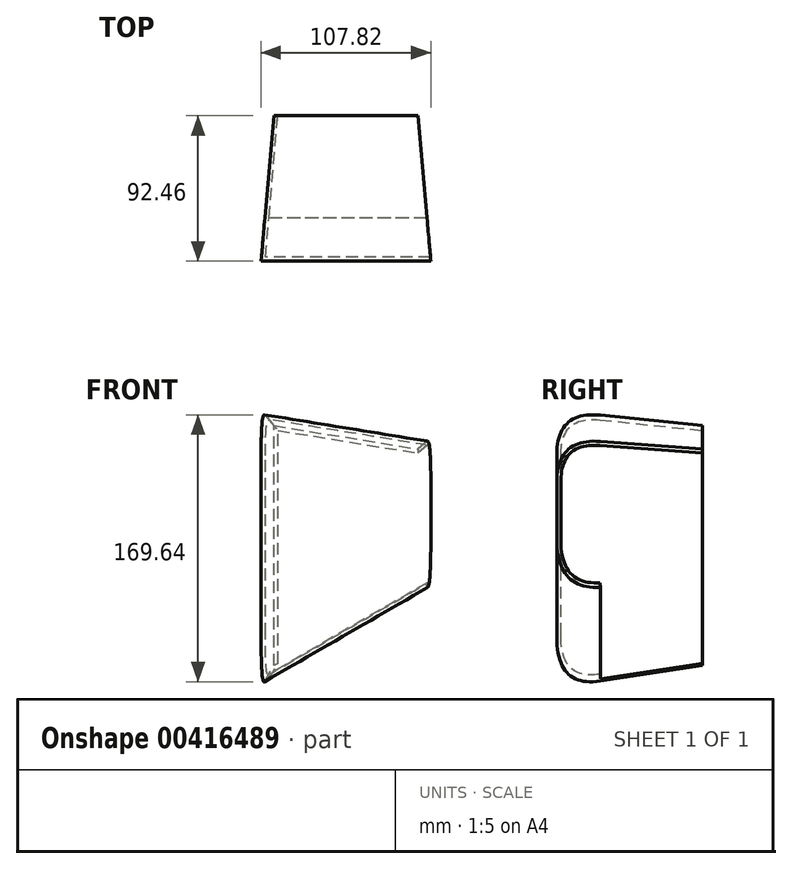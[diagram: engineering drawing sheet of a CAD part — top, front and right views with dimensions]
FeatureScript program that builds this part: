
annotation { "Feature Type Name" : "Feature", "Feature Type Description" : "" }
export const myFeature = defineFeature(function(context is Context, id is Id, definition is map)
    precondition{}
    {
        {
            var Q0;
            Q0=qCreatedBy(makeId("Front.planeOp"),FACE);
            var sketch = newSketch(context, id + "F0", { "sketchPlane" : qUnion([Q0])});
            skLineSegment(sketch, "E0", {"start": v(-53.03, 69.9) * mm, "end": v(38.61, 55.06) * mm});
            skLineSegment(sketch, "E1", {"start": v(38.61, 55.06) * mm, "end": v(38.61, -29.59) * mm});
            skLineSegment(sketch, "E2", {"start": v(38.61, -29.59) * mm, "end": v(-53.03, -82.5) * mm});
            skLineSegment(sketch, "E3", {"start": v(-53.03, -82.5) * mm, "end": v(-53.03, 69.9) * mm});
            skSolve(sketch);
        }
        {
            var Q0;
            Q0 = qSketchRegion(id + "F0", true);
            extrude(context, id + "F1", {"entities" : qUnion([Q0]), "depth" : 92.46 * mm, "hasDraft" : true, "draftAngle" : 5 * degree});
        }
        {
            var Q0;
            Q0=makeQuery(id+"F1.opExtrude","CAP_EDGE",EDGE,{"disambiguationData":[OSD([sQuery(id+"F0.wireOp",EDGE,"E0")])],"isStart":false});
            var Q1;
            Q1=makeQuery(id+"F1.opExtrude","CAP_EDGE",EDGE,{"disambiguationData":[OSD([sQuery(id+"F0.wireOp",EDGE,"E2")])],"isStart":false});
            fillet(context, id + "F2", {"entities" : qUnion([Q0, Q1]), "radius" : 25.4 * mm, "tangentPropagation" : true, "rho" : 0.5, "crossSection" : FilletCrossSection.CONIC, "allowEdgeOverflow" : false});
        }
        {
            var Q0;
            Q0=makeQuery(id+"F1.opExtrude","SWEPT_FACE",FACE,{"disambiguationData":[OSD([sQuery(id+"F0.wireOp",EDGE,"E2")])]});
            var Q1;
            Q1=makeQuery(id+"F1.opExtrude","SWEPT_FACE",FACE,{"disambiguationData":[OSD([sQuery(id+"F0.wireOp",EDGE,"E1")])]});
            var Q2;
            Q2=makeQuery(id+"F1.opExtrude","CAP_FACE",FACE,{"disambiguationData":[OSD([sQuery(id+"F0.wireOp",EDGE,"E0"),sQuery(id+"F0.wireOp",EDGE,"E1"),sQuery(id+"F0.wireOp",EDGE,"E2"),sQuery(id+"F0.wireOp",EDGE,"E3")])],"isStart":true});
            shell(context, id + "F3", {"entities" : qUnion([Q0, Q1, Q2]), "thickness" : 2.54 * mm});
        }
    });
